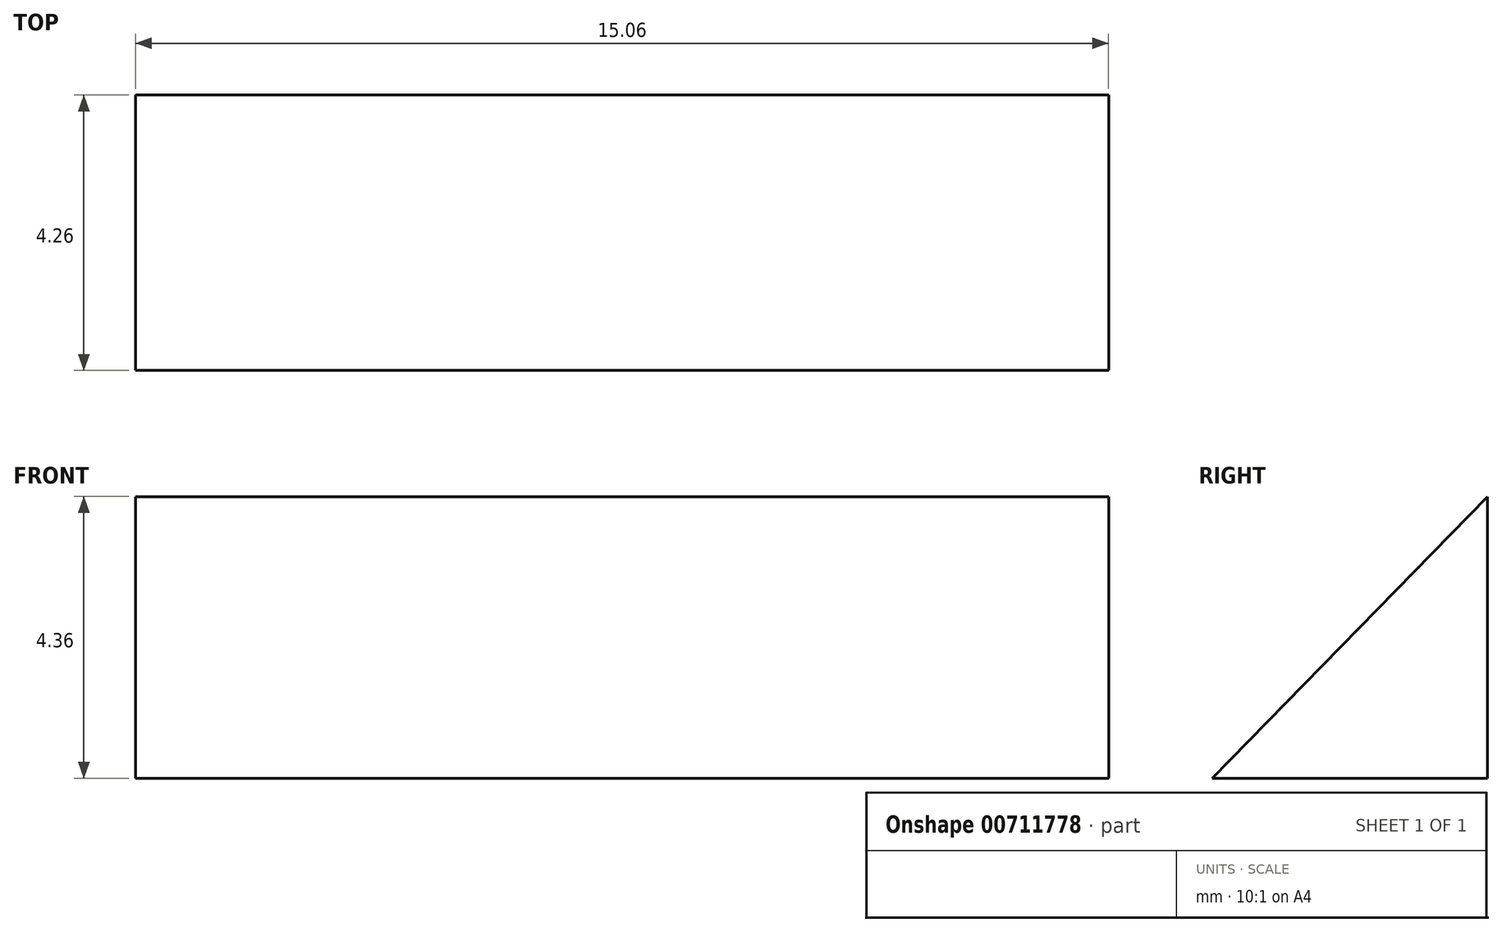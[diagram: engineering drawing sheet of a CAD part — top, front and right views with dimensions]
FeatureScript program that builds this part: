
annotation { "Feature Type Name" : "Feature", "Feature Type Description" : "" }
export const myFeature = defineFeature(function(context is Context, id is Id, definition is map)
    precondition{}
    {
        {
            var Q0;
            Q0=qCreatedBy(makeId("Right.planeOp"),FACE);
            var sketch = newSketch(context, id + "F0", { "sketchPlane" : qUnion([Q0])});
            skLineSegment(sketch, "E0.top", {"start": v(-96.87, 19.28) * mm, "end": v(-92.6, 19.28) * mm});
            skLineSegment(sketch, "E0.right", {"start": v(-92.6, 23.64) * mm, "end": v(-92.6, 19.28) * mm});
            skLineSegment(sketch, "E1", {"start": v(-96.87, 19.28) * mm, "end": v(-92.6, 23.64) * mm});
            skSolve(sketch);
        }
        {
            var Q0;
            Q0 = qSketchRegion(id + "F0", true);
            extrude(context, id + "F1", {"entities" : qUnion([Q0]), "depth" : 15.06 * mm, "offsetDistance" : 25.4 * mm});
        }
    });
